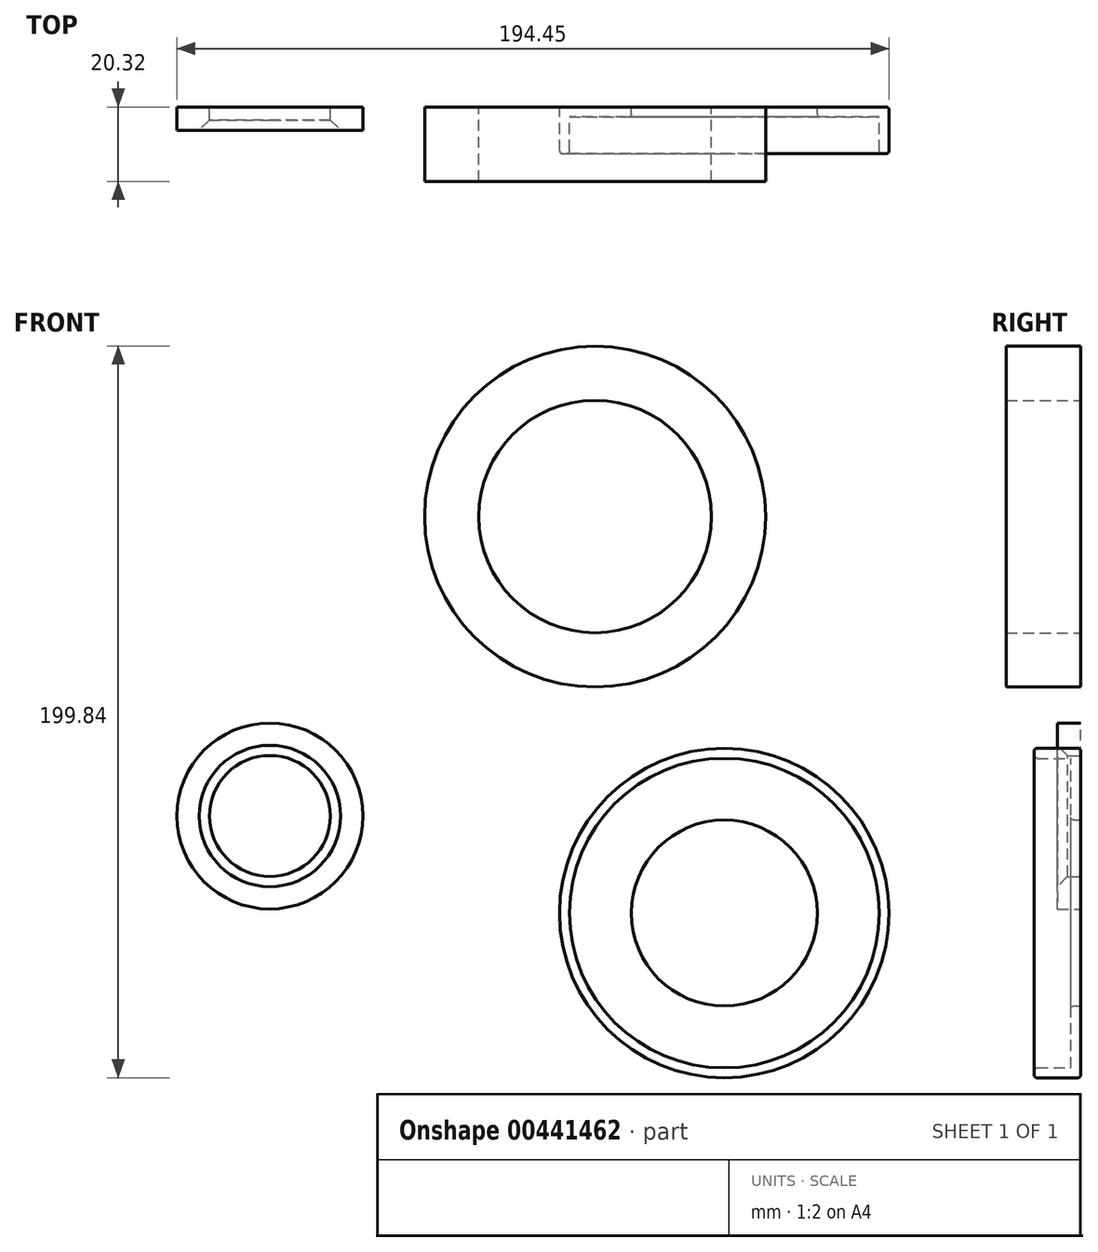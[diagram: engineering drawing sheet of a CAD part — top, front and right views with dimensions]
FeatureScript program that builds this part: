
annotation { "Feature Type Name" : "Feature", "Feature Type Description" : "" }
export const myFeature = defineFeature(function(context is Context, id is Id, definition is map)
    precondition{}
    {
        {
            var Q0;
            Q0=qCreatedBy(makeId("Front.planeOp"),FACE);
            var sketch = newSketch(context, id + "F0", { "sketchPlane" : qUnion([Q0])});
            skCircle(sketch, "E0", {"center": v(0, 0) * mm, "radius": 44.98 * mm});
            skCircle(sketch, "E1", {"center": v(0, 0) * mm, "radius": 38.63 * mm});
            skSolve(sketch);
        }
        {
            var Q0;
            Q0=makeQuery(id+"F0.imprint","IMPRINT",FACE,{"disambiguationData":[TD([[makeQuery(id+"F0.imprint","IMPRINT",EDGE,{"derivedFrom":sQuery(id+"F0.wireOp",EDGE,"E1")}),1.0]])]});
            var Q1;
            Q1=makeQuery(id+"F0.imprint","IMPRINT",FACE,{"disambiguationData":[TD([[makeQuery(id+"F0.imprint","IMPRINT",EDGE,{"derivedFrom":sQuery(id+"F0.wireOp",EDGE,"E0")}),1.0]])]});
            extrude(context, id + "F1", {"entities" : qUnion([Q0, Q1]), "depth" : 12.7 * mm});
        }
        {
            var Q0;
            Q0=makeQuery(id+"F1.opExtrude","CAP_FACE",FACE,{"disambiguationData":[OSD([sQuery(id+"F0.wireOp",EDGE,"E0")])],"isStart":false});
            shell(context, id + "F2", {"entities" : qUnion([Q0]), "thickness" : 2.7 * mm});
        }
        {
            var Q0;
            Q0=makeQuery(id+"F1.opExtrude","CAP_FACE",FACE,{"disambiguationData":[OSD([sQuery(id+"F0.wireOp",EDGE,"E0")])],"isStart":true});
            var sketch = newSketch(context, id + "F3", { "sketchPlane" : qUnion([Q0])});
            skCircle(sketch, "E2", {"center": v(0, 0) * mm, "radius": 25.4 * mm});
            skSolve(sketch);
        }
        {
            var Q0;
            Q0=makeQuery(id+"F3.imprint","IMPRINT",FACE,{"disambiguationData":[TD([[makeQuery(id+"F3.imprint","IMPRINT",EDGE,{"derivedFrom":sQuery(id+"F3.wireOp",EDGE,"E2")}),1.0]])]});
            extrude(context, id + "F4", {"entities" : qUnion([Q0]), "operationType" : NewBodyOperationType.REMOVE, "oppositeDirection" : true, "depth" : 25.4 * mm});
        }
        {
            var Q0;
            Q0=makeQuery(id+"F1.opExtrude","CAP_EDGE",EDGE,{"disambiguationData":[OSD([sQuery(id+"F0.wireOp",EDGE,"E0")])],"isStart":false});
            var Q1;
            {var subQ0=sQuery(id+"F0.wireOp",EDGE,"E0");Q1=makeQuery(id+"F2.opShell","OFFSET_EDGE",EDGE,{"disambiguationData":[OSD([subQ0]),TDD([makeQuery(id+"F1.opExtrude","CAP_EDGE",EDGE,{"disambiguationData":[OSD([subQ0])],"isStart":false})])]});}
            var Q2;
            {var subQ0=sQuery(id+"F0.wireOp",EDGE,"E0");Q2=makeQuery(id+"F4.boolean.opBoolean","INTERSECT",EDGE,{"derivedFrom":[makeQuery(id+"F2.opShell","OFFSET_FACE",FACE,{"disambiguationData":[OSD([subQ0]),TDD([makeQuery(id+"F1.opExtrude","CAP_FACE",FACE,{"disambiguationData":[OSD([subQ0])],"isStart":true})])]}),makeQuery(id+"F4.opExtrude","SWEPT_FACE",FACE,{"disambiguationData":[OSD([sQuery(id+"F3.wireOp",EDGE,"E2")])]})]});}
            var Q3;
            Q3=makeQuery(id+"F1.opExtrude","CAP_EDGE",EDGE,{"disambiguationData":[OSD([sQuery(id+"F0.wireOp",EDGE,"E0")])],"isStart":true});
            var Q4;
            Q4=makeQuery(id+"F4.boolean.opBoolean","COPY",EDGE,{"derivedFrom":makeQuery(id+"F4.opExtrude","CAP_EDGE",EDGE,{"disambiguationData":[OSD([sQuery(id+"F3.wireOp",EDGE,"E2")])],"isStart":true})});
            fillet(context, id + "F5", {"entities" : qUnion([Q0, Q1, Q2, Q3, Q4]), "radius" : 0.76 * mm, "tangentPropagation" : true, "allowEdgeOverflow" : false});
        }
        {
            var Q0;
            Q0=qCreatedBy(makeId("Front.planeOp"),FACE);
            var sketch = newSketch(context, id + "F6", { "sketchPlane" : qUnion([Q0])});
            skCircle(sketch, "E3", {"center": v(-124.07, 26.52) * mm, "radius": 25.4 * mm});
            skCircle(sketch, "E4", {"center": v(-124.07, 26.52) * mm, "radius": 16.51 * mm});
            skSolve(sketch);
        }
        {
            var Q0;
            Q0=makeQuery(id+"F6.imprint","IMPRINT",FACE,{"disambiguationData":[TD([[makeQuery(id+"F6.imprint","IMPRINT",EDGE,{"derivedFrom":sQuery(id+"F6.wireOp",EDGE,"E3")}),1.0]])]});
            extrude(context, id + "F7", {"entities" : qUnion([Q0]), "depth" : 6.35 * mm});
        }
        {
            var Q0;
            Q0=makeQuery(id+"F7.opExtrude","CAP_EDGE",EDGE,{"disambiguationData":[OSD([sQuery(id+"F6.wireOp",EDGE,"E4")])],"isStart":false});
            chamfer(context, id + "F8", {"entities" : qUnion([Q0]), "width" : 2.8 * mm, "tangentPropagation" : true});
        }
        {
            var Q0;
            Q0=qCreatedBy(makeId("Front.planeOp"),FACE);
            var sketch = newSketch(context, id + "F9", { "sketchPlane" : qUnion([Q0])});
            skCircle(sketch, "E5", {"center": v(-35.29, 108.31) * mm, "radius": 46.55 * mm});
            skCircle(sketch, "E6", {"center": v(-35.29, 108.31) * mm, "radius": 31.75 * mm});
            skSolve(sketch);
        }
        {
            var Q0;
            Q0 = qSketchRegion(id + "F9", true);
            extrude(context, id + "F10", {"entities" : qUnion([Q0]), "depth" : 20.32 * mm});
        }
        {
            var Q0;
            Q0=qCreatedBy(makeId("Front.planeOp"),FACE);
            var sketch = newSketch(context, id + "F11", { "sketchPlane" : qUnion([Q0])});
            skLineSegment(sketch, "E7.bottom", {"start": v(113.45, 38.39) * mm, "end": v(158, 38.39) * mm});
            skLineSegment(sketch, "E7.top", {"start": v(113.45, -7.2) * mm, "end": v(158, -7.2) * mm});
            skLineSegment(sketch, "E7.left", {"start": v(113.45, 38.39) * mm, "end": v(113.45, -7.2) * mm});
            skLineSegment(sketch, "E7.right", {"start": v(158, 38.39) * mm, "end": v(158, -7.2) * mm});
            skSolve(sketch);
        }
        {
            var Q0;
            Q0=makeQuery(id+"F11.imprint","IMPRINT",FACE,{"disambiguationData":[TD([[makeQuery(id+"F11.imprint","IMPRINT",EDGE,{"derivedFrom":sQuery(id+"F11.wireOp",EDGE,"E7.bottom")}),-1.0]])]});
            extrude(context, id + "F12", {"entities" : qUnion([Q0]), "depth" : 25.4 * mm});
        }
        {
            var Q0;
            Q0=makeQuery(id+"F12.opExtrude","CAP_FACE",FACE,{"disambiguationData":[OSD([sQuery(id+"F11.wireOp",EDGE,"E7.bottom"),sQuery(id+"F11.wireOp",EDGE,"E7.top"),sQuery(id+"F11.wireOp",EDGE,"E7.left"),sQuery(id+"F11.wireOp",EDGE,"E7.right")])],"isStart":false});
            var sketch = newSketch(context, id + "F13", { "sketchPlane" : qUnion([Q0])});
            skPoint(sketch, "E8", {"position": v(135.73, 15.6) * mm});
            skPoint(sketch, "E8.positionSnap0", {"position": v(135.73, 38.39) * mm});
            skPoint(sketch, "E8.positionSnap1", {"position": v(158, 15.6) * mm});
            skSolve(sketch);
        }
        {
            var Q0;
            Q0=sQuery(id+"F13.wireOp",VERTEX,"E8");
            var Q1;
            Q1=makeQuery(id+"F12.opExtrude","SWEPT_BODY",BODY,{"disambiguationData":[OSD([sQuery(id+"F11.wireOp",EDGE,"E7.bottom"),sQuery(id+"F11.wireOp",EDGE,"E7.top"),sQuery(id+"F11.wireOp",EDGE,"E7.left"),sQuery(id+"F11.wireOp",EDGE,"E7.right")])]});
            hole(context, id + "F14", {"style" : HoleStyle.C_SINK, "endStyle" : HoleEndStyle.BLIND, "holeDiameter" : 25.4 * mm, "cSinkDiameter" : 37.75 * mm, "cSinkAngle" : 90 * degree, "holeDepth" : 50.8 * mm, "isTappedThrough" : true, "tappedDepth" : 12.7 * mm, "tapClearance" : 3, "startFromSketch" : true, "locations" : qUnion([Q0]), "scope" : qUnion([Q1])});
        }
        {
            var Q0;
            Q0=makeQuery(id+"F12.opExtrude","SWEPT_BODY",BODY,{"disambiguationData":[OSD([sQuery(id+"F11.wireOp",EDGE,"E7.bottom"),sQuery(id+"F11.wireOp",EDGE,"E7.top"),sQuery(id+"F11.wireOp",EDGE,"E7.left"),sQuery(id+"F11.wireOp",EDGE,"E7.right")])]});
            deleteBodies(context, id + "F15", {"entities" : qUnion([Q0])});
        }
    });
